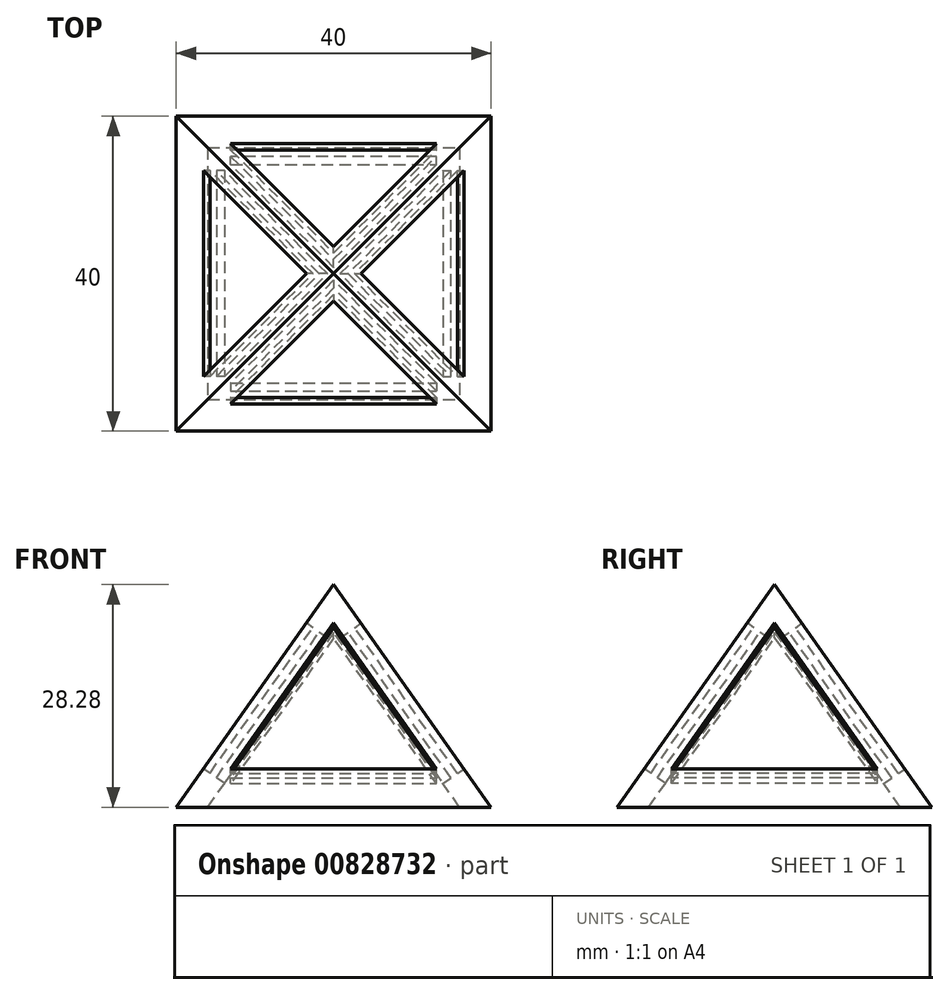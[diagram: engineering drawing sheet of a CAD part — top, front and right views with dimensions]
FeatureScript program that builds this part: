
annotation { "Feature Type Name" : "Feature", "Feature Type Description" : "" }
export const myFeature = defineFeature(function(context is Context, id is Id, definition is map)
    precondition{}
    {
        {
            assignVariable(context, id + "F0", {"name" : "Width", "anyValue" : 40});
        }
        {
            assignVariable(context, id + "F1", {"name" : "Hollow", "anyValue" : 32});
        }
        {
            var Q0;
            Q0=qCreatedBy(makeId("Top.planeOp"),FACE);
            var sketch = newSketch(context, id + "F2", { "sketchPlane" : qUnion([Q0])});
            skLineSegment(sketch, "E0.bottom", {"start": v(-20, 20) * mm, "end": v(20, 20) * mm});
            skLineSegment(sketch, "E0.top", {"start": v(-20, -20) * mm, "end": v(20, -20) * mm});
            skLineSegment(sketch, "E0.left", {"start": v(-20, 20) * mm, "end": v(-20, -20) * mm});
            skLineSegment(sketch, "E0.right", {"start": v(20, 20) * mm, "end": v(20, -20) * mm});
            skSolve(sketch);
        }
        {
            var Q0;
            Q0=makeQuery(id+"F2.imprint","IMPRINT",FACE,{"disambiguationData":[TD([[makeQuery(id+"F2.imprint","IMPRINT",EDGE,{"derivedFrom":sQuery(id+"F2.wireOp",EDGE,"E0.bottom")}),-1.0]])]});
            cPlane(context, id + "F3", {"entities" : qUnion([Q0]), "cplaneType" : CPlaneType.OFFSET, "offset" : (sqrt((sqrt((getVariable(context, 'Width') * getVariable(context, 'Width')) - ((getVariable(context, 'Width') / 2) * (getVariable(context, 'Width') / 2)))) * (sqrt((getVariable(context, 'Width') * getVariable(context, 'Width')) - ((getVariable(context, 'Width') / 2) * (getVariable(context, 'Width') / 2)))) - ((getVariable(context, 'Width') / 2) * (getVariable(context, 'Width') / 2)))) * mm, "width" : 150 * mm, "height" : 150 * mm});
        }
        {
            var Q0;
            Q0=qCreatedBy(id+"F3.planeOp",FACE);
            var sketch = newSketch(context, id + "F4", { "sketchPlane" : qUnion([Q0])});
            skPoint(sketch, "E1", {"position": v(0, 0) * mm});
            skSolve(sketch);
        }
        {
            var Q0;
            Q0=makeQuery(id+"F2.imprint","IMPRINT",FACE,{"disambiguationData":[TD([[makeQuery(id+"F2.imprint","IMPRINT",EDGE,{"derivedFrom":sQuery(id+"F2.wireOp",EDGE,"E0.bottom")}),-1.0]])]});
            var Q1;
            Q1=sQuery(id+"F4.wireOp",VERTEX,"E1");
            loft(context, id + "F5", {"sheetProfilesArray" : [{ "sheetProfileEntities" : qUnion([Q0]) }, { "sheetProfileEntities" : qUnion([Q1]) }]});
        }
        {
            var Q0;
            Q0=qCreatedBy(makeId("Top.planeOp"),FACE);
            cPlane(context, id + "F6", {"entities" : qUnion([Q0]), "cplaneType" : CPlaneType.OFFSET, "offset" : (sqrt((sqrt((getVariable(context, 'Hollow') * getVariable(context, 'Hollow')) - ((getVariable(context, 'Hollow') / 2) * (getVariable(context, 'Hollow') / 2)))) * (sqrt((getVariable(context, 'Hollow') * getVariable(context, 'Hollow')) - ((getVariable(context, 'Hollow') / 2) * (getVariable(context, 'Hollow') / 2)))) - ((getVariable(context, 'Hollow') / 2) * (getVariable(context, 'Hollow') / 2)))) * mm, "width" : 150 * mm, "height" : 150 * mm});
        }
        {
            var Q0;
            Q0=qCreatedBy(makeId("Top.planeOp"),FACE);
            var sketch = newSketch(context, id + "F7", { "sketchPlane" : qUnion([Q0])});
            skLineSegment(sketch, "E2.bottom", {"start": v(-16, 16) * mm, "end": v(16, 16) * mm});
            skLineSegment(sketch, "E2.top", {"start": v(-16, -16) * mm, "end": v(16, -16) * mm});
            skLineSegment(sketch, "E2.left", {"start": v(-16, 16) * mm, "end": v(-16, -16) * mm});
            skLineSegment(sketch, "E2.right", {"start": v(16, 16) * mm, "end": v(16, -16) * mm});
            skSolve(sketch);
        }
        {
            var Q0;
            Q0=qCreatedBy(id+"F6.planeOp",FACE);
            var sketch = newSketch(context, id + "F8", { "sketchPlane" : qUnion([Q0])});
            skPoint(sketch, "E3", {"position": v(0, 0) * mm});
            skSolve(sketch);
        }
        {
            var Q1;
            Q1=makeQuery(id+"F7.imprint","IMPRINT",FACE,{"disambiguationData":[TD([[makeQuery(id+"F7.imprint","IMPRINT",EDGE,{"derivedFrom":sQuery(id+"F7.wireOp",EDGE,"E2.bottom")}),-1.0]])]});
            var Q2;
            Q2=sQuery(id+"F8.wireOp",VERTEX,"E3");
            loft(context, id + "F9", {"operationType" : NewBodyOperationType.REMOVE, "sheetProfilesArray" : [{ "sheetProfileEntities" : qUnion([Q1]) }, { "sheetProfileEntities" : qUnion([Q2]) }]});
        }
        {
            var Q0;
            Q0=makeQuery(id+"F5.opLoft","SWEPT_FACE",FACE,{"disambiguationData":[OSD([sQuery(id+"F2.wireOp",EDGE,"E0.top"),sQuery(id+"F2.wireOp",EDGE,"E0.left"),sQuery(id+"F2.wireOp",EDGE,"E0.right")])]});
            cPlane(context, id + "F10", {"entities" : qUnion([Q0]), "cplaneType" : CPlaneType.OFFSET, "offset" : 0 * mm, "width" : 150 * mm, "height" : 150 * mm});
        }
        {
            var Q0;
            Q0=makeQuery(id+"F5.opLoft","SWEPT_FACE",FACE,{"disambiguationData":[OSD([sQuery(id+"F2.wireOp",EDGE,"E0.bottom"),sQuery(id+"F2.wireOp",EDGE,"E0.top"),sQuery(id+"F2.wireOp",EDGE,"E0.left")])]});
            cPlane(context, id + "F11", {"entities" : qUnion([Q0]), "cplaneType" : CPlaneType.OFFSET, "offset" : 0 * mm, "width" : 150 * mm, "height" : 150 * mm});
        }
        {
            var Q0;
            Q0=qCreatedBy(id+"F10.planeOp",FACE);
            var sketch = newSketch(context, id + "F12", { "sketchPlane" : qUnion([Q0])});
            skLineSegment(sketch, "E4", {"start": v(0, 17.1) * mm, "end": v(-13.07, -5.55) * mm});
            skLineSegment(sketch, "E5", {"start": v(-13.07, -5.55) * mm, "end": v(13.07, -5.55) * mm});
            skLineSegment(sketch, "E6", {"start": v(13.07, -5.55) * mm, "end": v(0, 17.1) * mm});
            skSolve(sketch);
        }
        {
            var Q0;
            Q0 = qSketchRegion(id + "F12", true);
            extrude(context, id + "F13", {"entities" : qUnion([Q0]), "operationType" : NewBodyOperationType.REMOVE, "depth" : -1 * mm, "offsetDistance" : 25 * mm});
        }
        {
            var Q0;
            Q0 = qSketchRegion(id + "F12", true);
            extrude(context, id + "F14", {"entities" : qUnion([Q0]), "operationType" : NewBodyOperationType.REMOVE, "oppositeDirection" : true, "depth" : 5 * mm, "offsetDistance" : 25 * mm, "hasSecondDirection" : true, "secondDirectionOppositeDirection" : false, "secondDirectionDepth" : -2 * mm});
        }
        {
            var Q0;
            Q0=qCreatedBy(id+"F11.planeOp",FACE);
            var sketch = newSketch(context, id + "F15", { "sketchPlane" : qUnion([Q0])});
            skLineSegment(sketch, "E7", {"start": v(0, 17.1) * mm, "end": v(-13.07, -5.55) * mm});
            skLineSegment(sketch, "E8", {"start": v(-13.07, -5.55) * mm, "end": v(13.07, -5.55) * mm});
            skLineSegment(sketch, "E9", {"start": v(13.07, -5.55) * mm, "end": v(0, 17.1) * mm});
            skSolve(sketch);
        }
        {
            var Q0;
            Q0 = qSketchRegion(id + "F15", true);
            extrude(context, id + "F16", {"entities" : qUnion([Q0]), "operationType" : NewBodyOperationType.REMOVE, "oppositeDirection" : true, "depth" : 1 * mm, "offsetDistance" : 25 * mm});
        }
        {
            var Q0;
            Q0 = qSketchRegion(id + "F15", true);
            extrude(context, id + "F17", {"entities" : qUnion([Q0]), "operationType" : NewBodyOperationType.REMOVE, "oppositeDirection" : true, "depth" : 5 * mm, "offsetDistance" : 25 * mm, "hasSecondDirection" : true, "secondDirectionOppositeDirection" : false, "secondDirectionDepth" : -2 * mm});
        }
        {
            var Q0;
            Q0=makeQuery(id+"F5.opLoft","SWEPT_FACE",FACE,{"disambiguationData":[OSD([sQuery(id+"F2.wireOp",EDGE,"E0.bottom"),sQuery(id+"F2.wireOp",EDGE,"E0.left"),sQuery(id+"F2.wireOp",EDGE,"E0.right")])]});
            var sketch = newSketch(context, id + "F18", { "sketchPlane" : qUnion([Q0])});
            skLineSegment(sketch, "E10", {"start": v(0, 17.1) * mm, "end": v(-13.07, -5.55) * mm});
            skLineSegment(sketch, "E11", {"start": v(-13.07, -5.55) * mm, "end": v(13.07, -5.55) * mm});
            skLineSegment(sketch, "E12", {"start": v(13.07, -5.55) * mm, "end": v(0, 17.1) * mm});
            skSolve(sketch);
        }
        {
            var Q0;
            Q0 = qSketchRegion(id + "F18", true);
            extrude(context, id + "F19", {"entities" : qUnion([Q0]), "operationType" : NewBodyOperationType.REMOVE, "oppositeDirection" : true, "depth" : 1 * mm, "offsetDistance" : 25 * mm});
        }
        {
            var Q0;
            Q0 = qSketchRegion(id + "F18", true);
            extrude(context, id + "F20", {"entities" : qUnion([Q0]), "operationType" : NewBodyOperationType.REMOVE, "depth" : -5 * mm, "offsetDistance" : 25 * mm, "hasSecondDirection" : true, "secondDirectionOppositeDirection" : true, "secondDirectionDepth" : 2 * mm});
        }
        {
            var Q0;
            Q0=makeQuery(id+"F5.opLoft","SWEPT_FACE",FACE,{"disambiguationData":[OSD([sQuery(id+"F2.wireOp",EDGE,"E0.bottom"),sQuery(id+"F2.wireOp",EDGE,"E0.top"),sQuery(id+"F2.wireOp",EDGE,"E0.right")])]});
            var sketch = newSketch(context, id + "F21", { "sketchPlane" : qUnion([Q0])});
            skLineSegment(sketch, "E13", {"start": v(0, 17.1) * mm, "end": v(-13.07, -5.55) * mm});
            skLineSegment(sketch, "E14", {"start": v(-13.07, -5.55) * mm, "end": v(13.07, -5.55) * mm});
            skLineSegment(sketch, "E15", {"start": v(13.07, -5.55) * mm, "end": v(0, 17.1) * mm});
            skSolve(sketch);
        }
        {
            var Q0;
            Q0 = qSketchRegion(id + "F21", true);
            extrude(context, id + "F22", {"entities" : qUnion([Q0]), "operationType" : NewBodyOperationType.REMOVE, "oppositeDirection" : true, "depth" : 1 * mm, "offsetDistance" : 25 * mm});
        }
        {
            var Q0;
            Q0 = qSketchRegion(id + "F21", true);
            extrude(context, id + "F23", {"entities" : qUnion([Q0]), "operationType" : NewBodyOperationType.REMOVE, "oppositeDirection" : true, "depth" : 5 * mm, "offsetDistance" : 25 * mm, "hasSecondDirection" : true, "secondDirectionOppositeDirection" : false, "secondDirectionDepth" : -2 * mm});
        }
    });
